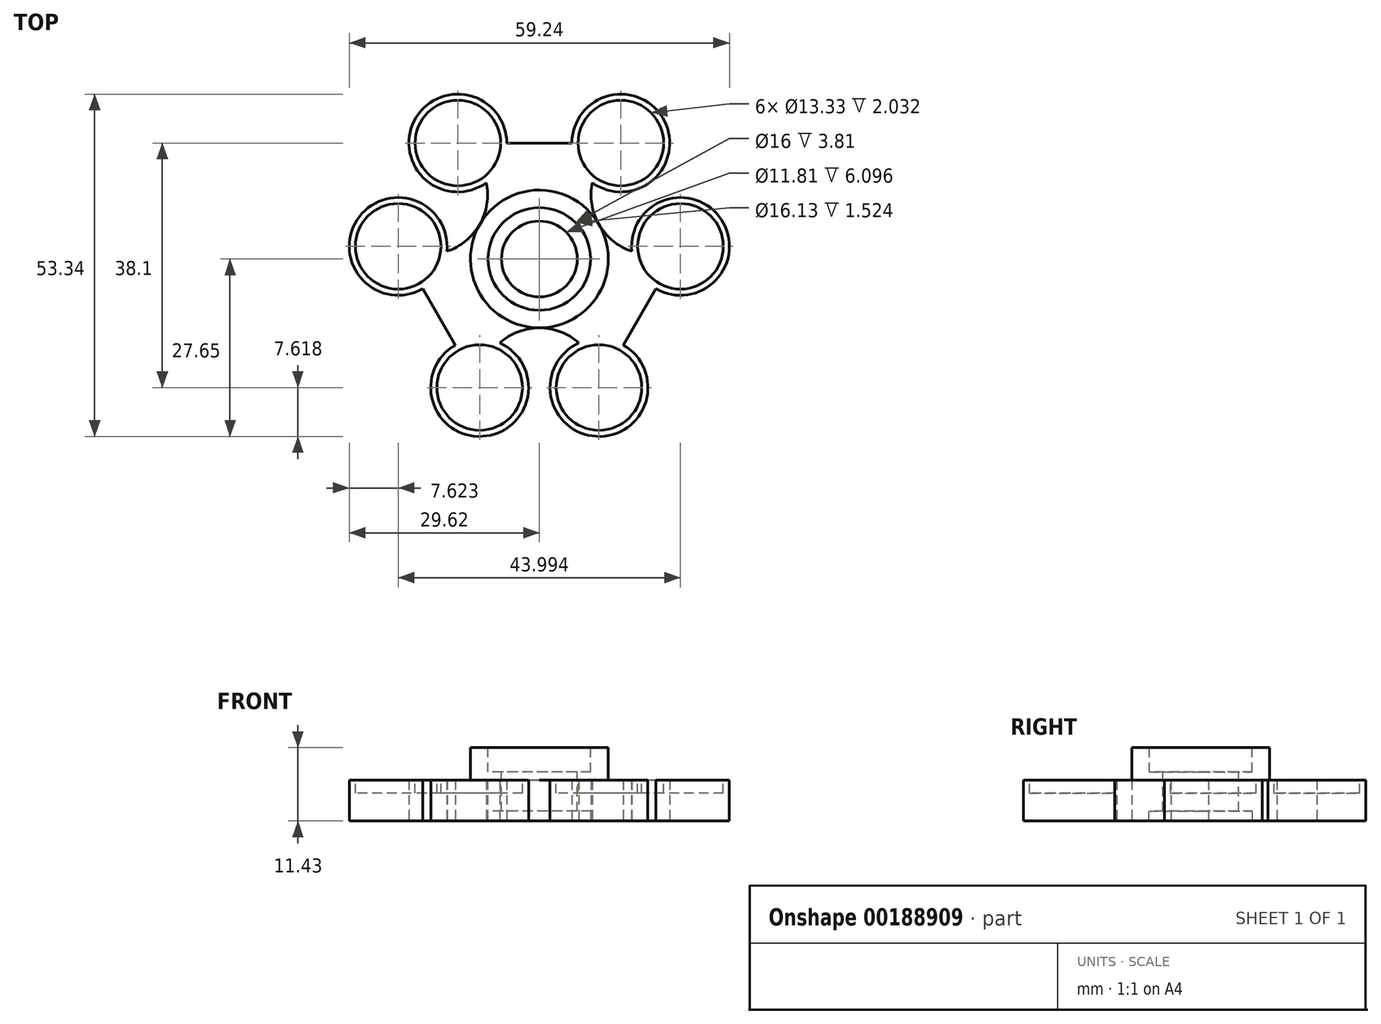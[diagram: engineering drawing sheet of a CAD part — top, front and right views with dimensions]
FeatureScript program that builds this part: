
annotation { "Feature Type Name" : "Feature", "Feature Type Description" : "" }
export const myFeature = defineFeature(function(context is Context, id is Id, definition is map)
    precondition{}
    {
        {
            var Q0;
            Q0=qCreatedBy(makeId("Top.planeOp"),FACE);
            var sketch = newSketch(context, id + "F0", { "sketchPlane" : qUnion([Q0])});
            skLineSegment(sketch, "E0", {"start": v(-12.7, 18.07) * mm, "end": v(12.7, 18.07) * mm});
            skLineSegment(sketch, "E1", {"start": v(9.3, -20.03) * mm, "end": v(22, 1.96) * mm});
            skLineSegment(sketch, "E2", {"start": v(-22, 1.96) * mm, "end": v(-9.3, -20.03) * mm});
            skLineSegment(sketch, "E3", {"start": v(0, 18.07) * mm, "end": v(0, 0) * mm, "construction": true});
            skLineSegment(sketch, "E4", {"start": v(0, 0) * mm, "end": v(15.65, -9.03) * mm, "construction": true});
            skLineSegment(sketch, "E5", {"start": v(-15.65, -9.03) * mm, "end": v(0, 0) * mm, "construction": true});
            skArc(sketch, "E6", {"start": v(-22, 1.96) * mm, "mid": v(-9.3, 5.37) * mm, "end": v(-12.7, 18.07) * mm});
            skArc(sketch, "E7", {"start": v(9.3, -20.03) * mm, "mid": v(0, -10.74) * mm, "end": v(-9.3, -20.03) * mm});
            skArc(sketch, "E8", {"start": v(12.7, 18.07) * mm, "mid": v(9.3, 5.37) * mm, "end": v(22, 1.96) * mm});
            skLineSegment(sketch, "E9", {"start": v(-12.7, 18.07) * mm, "end": v(-22, 1.96) * mm, "construction": true});
            skLineSegment(sketch, "E10", {"start": v(-9.3, -20.03) * mm, "end": v(9.3, -20.03) * mm, "construction": true});
            skLineSegment(sketch, "E11", {"start": v(22, 1.96) * mm, "end": v(12.7, 18.07) * mm, "construction": true});
            skCircle(sketch, "E12", {"center": v(-12.7, 18.07) * mm, "radius": 7.62 * mm});
            skCircle(sketch, "E13", {"center": v(12.7, 18.07) * mm, "radius": 7.62 * mm});
            skCircle(sketch, "E14", {"center": v(22, 1.96) * mm, "radius": 7.62 * mm});
            skCircle(sketch, "E15", {"center": v(9.3, -20.03) * mm, "radius": 7.62 * mm});
            skCircle(sketch, "E16", {"center": v(-22, 1.96) * mm, "radius": 7.62 * mm});
            skCircle(sketch, "E17", {"center": v(-9.3, -20.03) * mm, "radius": 7.62 * mm});
            skSolve(sketch);
        }
        {
            var Q0;
            Q0=qSketchRegion(id+"F0",true);
            extrude(context, id + "F1", {"entities" : qUnion([Q0]), "depth" : 6.35 * mm});
        }
        {
            var Q0;
            Q0=makeQuery(id+"F1.opExtrude","CAP_FACE",FACE,{"disambiguationData":[OSD([sQuery(id+"F0.wireOp",EDGE,"E0"),sQuery(id+"F0.wireOp",EDGE,"E1"),sQuery(id+"F0.wireOp",EDGE,"E2"),sQuery(id+"F0.wireOp",EDGE,"E6"),sQuery(id+"F0.wireOp",EDGE,"E7"),sQuery(id+"F0.wireOp",EDGE,"E8"),sQuery(id+"F0.wireOp",EDGE,"E12"),sQuery(id+"F0.wireOp",EDGE,"E13"),sQuery(id+"F0.wireOp",EDGE,"E14"),sQuery(id+"F0.wireOp",EDGE,"E15"),sQuery(id+"F0.wireOp",EDGE,"E16"),sQuery(id+"F0.wireOp",EDGE,"E17")])],"isStart":false});
            var sketch = newSketch(context, id + "F2", { "sketchPlane" : qUnion([Q0])});
            skCircle(sketch, "E18", {"center": v(12.7, 18.07) * mm, "radius": 6.67 * mm});
            skCircle(sketch, "E19", {"center": v(22, 1.96) * mm, "radius": 6.67 * mm});
            skCircle(sketch, "E20", {"center": v(9.3, -20.03) * mm, "radius": 6.67 * mm});
            skCircle(sketch, "E21", {"center": v(-9.3, -20.03) * mm, "radius": 6.67 * mm});
            skCircle(sketch, "E22", {"center": v(-22, 1.96) * mm, "radius": 6.67 * mm});
            skCircle(sketch, "E23", {"center": v(-12.7, 18.07) * mm, "radius": 6.67 * mm});
            skSolve(sketch);
        }
        {
            var Q0;
            Q0=qSketchRegion(id+"F2",true);
            extrude(context, id + "F3", {"entities" : qUnion([Q0]), "operationType" : NewBodyOperationType.REMOVE, "oppositeDirection" : true, "depth" : 2.03 * mm});
        }
        {
            var Q0;
            Q0=makeQuery(id+"F1.opExtrude","CAP_FACE",FACE,{"disambiguationData":[OSD([sQuery(id+"F0.wireOp",EDGE,"E0"),sQuery(id+"F0.wireOp",EDGE,"E1"),sQuery(id+"F0.wireOp",EDGE,"E2"),sQuery(id+"F0.wireOp",EDGE,"E6"),sQuery(id+"F0.wireOp",EDGE,"E7"),sQuery(id+"F0.wireOp",EDGE,"E8"),sQuery(id+"F0.wireOp",EDGE,"E12"),sQuery(id+"F0.wireOp",EDGE,"E13"),sQuery(id+"F0.wireOp",EDGE,"E14"),sQuery(id+"F0.wireOp",EDGE,"E15"),sQuery(id+"F0.wireOp",EDGE,"E16"),sQuery(id+"F0.wireOp",EDGE,"E17")])],"isStart":false});
            var sketch = newSketch(context, id + "F4", { "sketchPlane" : qUnion([Q0])});
            skCircle(sketch, "E24", {"center": v(0, 0) * mm, "radius": 10.74 * mm});
            skSolve(sketch);
        }
        {
            var Q0;
            Q0=qSketchRegion(id+"F4",true);
            extrude(context, id + "F5", {"entities" : qUnion([Q0]), "operationType" : NewBodyOperationType.ADD, "depth" : 5.08 * mm});
        }
        {
            var Q0;
            Q0=makeQuery(id+"F5.opExtrude","CAP_FACE",FACE,{"disambiguationData":[OSD([sQuery(id+"F4.wireOp",EDGE,"E24")])],"isStart":false});
            var sketch = newSketch(context, id + "F6", { "sketchPlane" : qUnion([Q0])});
            skCircle(sketch, "E25", {"center": v(0, 0) * mm, "radius": 8 * mm});
            skSolve(sketch);
        }
        {
            var Q0;
            Q0=qSketchRegion(id+"F6",true);
            extrude(context, id + "F7", {"entities" : qUnion([Q0]), "operationType" : NewBodyOperationType.REMOVE, "oppositeDirection" : true, "depth" : 3.8 * mm});
        }
        {
            var Q0;
            Q0=makeQuery(id+"F7.boolean.opBoolean","COPY",FACE,{"derivedFrom":makeQuery(id+"F7.opExtrude","CAP_FACE",FACE,{"disambiguationData":[OSD([sQuery(id+"F6.wireOp",EDGE,"E25")])],"isStart":false})});
            var sketch = newSketch(context, id + "F8", { "sketchPlane" : qUnion([Q0])});
            skCircle(sketch, "E26", {"center": v(0, 0) * mm, "radius": 5.9 * mm});
            skSolve(sketch);
        }
        {
            var Q0;
            Q0=qSketchRegion(id+"F8",true);
            extrude(context, id + "F9", {"entities" : qUnion([Q0]), "operationType" : NewBodyOperationType.REMOVE, "oppositeDirection" : true, "depth" : 6.1 * mm});
        }
        {
            var Q0;
            Q0=makeQuery(id+"F9.boolean.opBoolean","COPY",FACE,{"derivedFrom":makeQuery(id+"F9.opExtrude","CAP_FACE",FACE,{"disambiguationData":[OSD([sQuery(id+"F8.wireOp",EDGE,"E26")])],"isStart":false})});
            var sketch = newSketch(context, id + "F10", { "sketchPlane" : qUnion([Q0])});
            skCircle(sketch, "E27", {"center": v(0, 0) * mm, "radius": 8.06 * mm});
            skSolve(sketch);
        }
        {
            var Q0;
            Q0=qSketchRegion(id+"F10",true);
            extrude(context, id + "F11", {"entities" : qUnion([Q0]), "operationType" : NewBodyOperationType.REMOVE, "oppositeDirection" : true, "depth" : 25.4 * mm});
        }
    });
